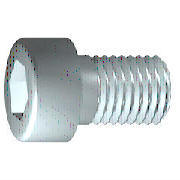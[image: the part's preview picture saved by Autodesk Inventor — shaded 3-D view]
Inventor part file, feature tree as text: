
AUTODESK INVENTOR PART (.ipt)
format: ipt  version: 2017.1 (Build 211199000, 199)  size: 182,784 bytes
history: native  units: mm (DEFAULTED — no unit token found)
features: sketch x2, extrude x1, plane x1, fillet x1
ambient origin geometry x7: Origin, YZ Plane, XY Plane, X Axis, Y Axis, Z Axis, Center Point
bodies: Solid1 (feature_tree), Body (feature_tree)
feature tree (5):
  extrude  "Slot"  Depth=1.5876mm
  plane  "Work Plane1"
  fillet  "Fillet2"  Radius=3.175mm
  sketch  "Sketch1"  dims[d1=19.05mm d2=1.5876mm d3=3.175mm]
  sketch  "Sketch2"  dims[d4=1.4478mm d5=60.0deg d6=3.175mm d7=3.175mm d8=2.756963mm d9=5.207mm d10=90.0deg d11=10.0mm d12=0.0mm d13=19.05mm d14=0.0mm d15=0.37846mm d16=0.37846mm d17=0.3048mm d19=0.0mm d26=38.1mm d27=45.0deg d28=0.0mm d29=0.0mm d30=0.127mm]
